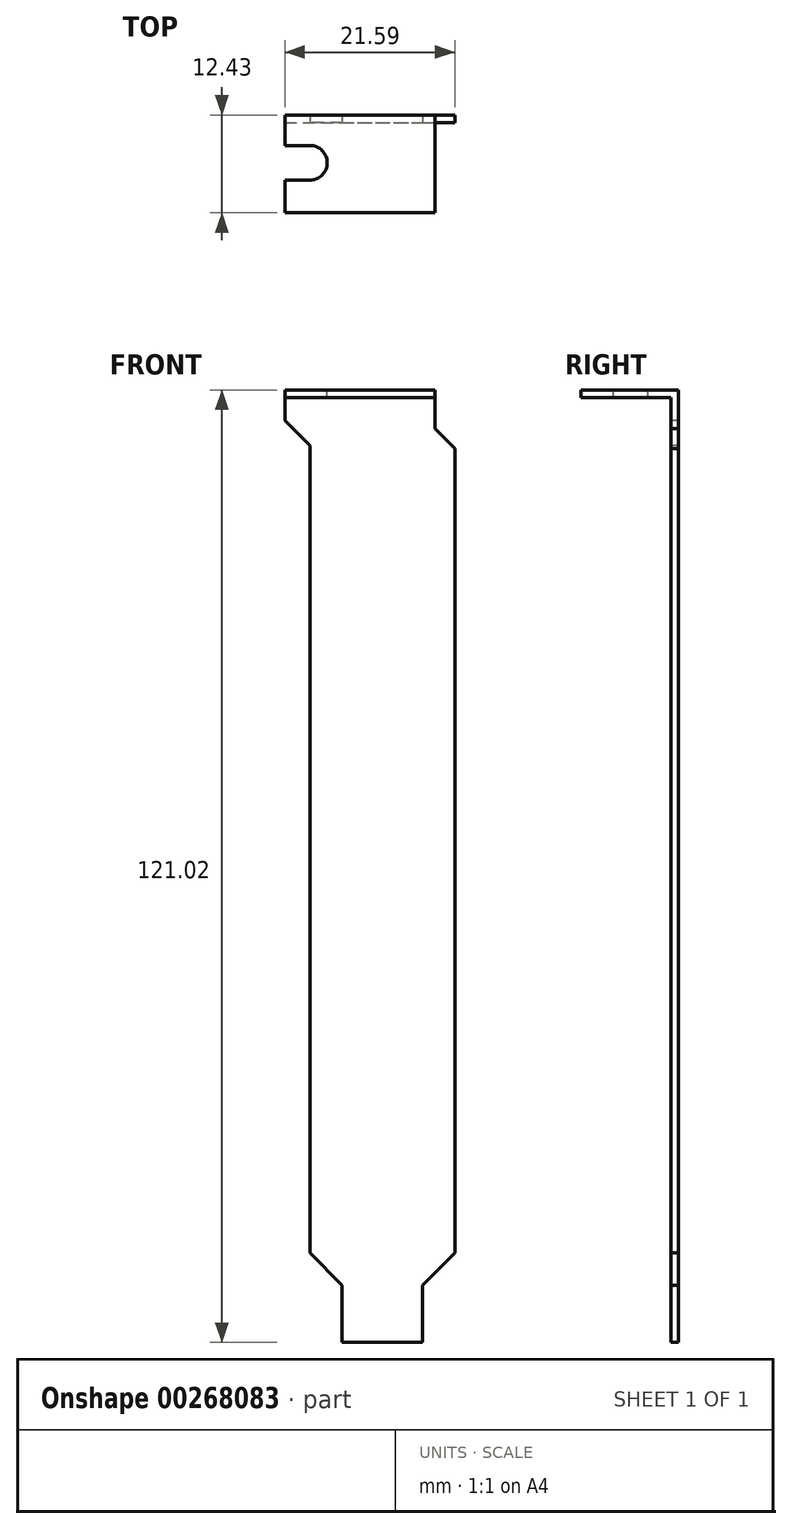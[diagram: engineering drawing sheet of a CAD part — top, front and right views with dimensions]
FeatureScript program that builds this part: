
annotation { "Feature Type Name" : "Feature", "Feature Type Description" : "" }
export const myFeature = defineFeature(function(context is Context, id is Id, definition is map)
    precondition{}
    {
        {
            assignVariable(context, id + "F0", {"name" : "BracketThickness", "anyValue" : 1 * mm});
        }
        {
            var Q0;
            Q0=qCreatedBy(makeId("Front.planeOp"),FACE);
            var sketch = newSketch(context, id + "F1", { "sketchPlane" : qUnion([Q0])});
            skLineSegment(sketch, "E0", {"start": v(-5.1, 0) * mm, "end": v(5.1, 0) * mm});
            skLineSegment(sketch, "E1", {"start": v(-5.1, 0) * mm, "end": v(-5.1, 7.27) * mm});
            skLineSegment(sketch, "E2", {"start": v(5.1, 0) * mm, "end": v(5.1, 7.27) * mm});
            skLineSegment(sketch, "E3", {"start": v(5.1, 7.27) * mm, "end": v(-5.1, 7.27) * mm, "construction": true});
            skLineSegment(sketch, "E4", {"start": v(-5.1, 7.27) * mm, "end": v(-9.21, 11.38) * mm});
            skLineSegment(sketch, "E5", {"start": v(-9.21, 11.38) * mm, "end": v(-9.21, 113.93) * mm});
            skLineSegment(sketch, "E6", {"start": v(5.1, 7.27) * mm, "end": v(9.2, 11.38) * mm});
            skLineSegment(sketch, "E7", {"start": v(9.2, 11.38) * mm, "end": v(9.2, 113.54) * mm});
            skLineSegment(sketch, "E8", {"start": v(9.21, 113.54) * mm, "end": v(6.67, 116.08) * mm});
            skLineSegment(sketch, "E9", {"start": v(6.67, 116.08) * mm, "end": v(6.67, 120.02) * mm});
            skLineSegment(sketch, "E10", {"start": v(6.67, 120.02) * mm, "end": v(-12.38, 120.02) * mm, "construction": true});
            skLineSegment(sketch, "E11", {"start": v(-12.38, 120.02) * mm, "end": v(-12.38, 117.1) * mm});
            skLineSegment(sketch, "E12", {"start": v(-12.38, 117.1) * mm, "end": v(-9.21, 113.93) * mm});
            skLineSegment(sketch, "E13", {"start": v(-9.21, 11.38) * mm, "end": v(9.2, 11.38) * mm, "construction": true});
            skLineSegment(sketch, "E14", {"start": v(-12.38, 120.02) * mm, "end": v(-12.38, 121.02) * mm});
            skLineSegment(sketch, "E15", {"start": v(-12.38, 121.02) * mm, "end": v(6.67, 121.02) * mm});
            skLineSegment(sketch, "E16", {"start": v(6.67, 121.02) * mm, "end": v(6.67, 120.02) * mm});
            skSolve(sketch);
        }
        {
            var Q0;
            Q0=makeQuery(id+"F1.imprint","IMPRINT",FACE,{"disambiguationData":[TD([[makeQuery(id+"F1.imprint","IMPRINT",EDGE,{"derivedFrom":sQuery(id+"F1.wireOp",EDGE,"E0")}),1.0]])]});
            extrude(context, id + "F2", {"entities" : qUnion([Q0]), "oppositeDirection" : true, "depth" : getVariable(context, 'BracketThickness')});
        }
        {
            var Q0;
            Q0=makeQuery(id+"F2.opExtrude","SWEPT_FACE",FACE,{"disambiguationData":[OSD([sQuery(id+"F1.wireOp",EDGE,"E15")])]});
            var sketch = newSketch(context, id + "F3", { "sketchPlane" : qUnion([Q0])});
            skLineSegment(sketch, "E17.bottom", {"start": v(-12.38, 0) * mm, "end": v(6.67, 0) * mm});
            skLineSegment(sketch, "E17.top", {"start": v(-12.38, -11.43) * mm, "end": v(6.67, -11.43) * mm});
            skLineSegment(sketch, "E17.left", {"start": v(-12.38, 0) * mm, "end": v(-12.38, -11.43) * mm});
            skLineSegment(sketch, "E17.right", {"start": v(6.67, 0) * mm, "end": v(6.67, -11.43) * mm});
            skLineSegment(sketch, "E18", {"start": v(-12.38, -2.87) * mm, "end": v(-9.2, -2.87) * mm});
            skLineSegment(sketch, "E19", {"start": v(-9.2, -2.87) * mm, "end": v(-9.2, -7.3) * mm, "construction": true});
            skLineSegment(sketch, "E20", {"start": v(-9.2, -7.3) * mm, "end": v(-12.38, -7.3) * mm});
            skArc(sketch, "E21", {"start": v(-9.2, -2.87) * mm, "mid": v(-7, -5.08) * mm, "end": v(-9.2, -7.3) * mm});
            skSolve(sketch);
        }
        {
            var Q0;
            {var subQ1=sQuery(id+"F3.wireOp",EDGE,"E17.bottom");Q0=makeQuery(id+"F3.imprint","IMPRINT",FACE,{"disambiguationData":[TD([[makeQuery(id+"F3.imprint","IMPRINT",EDGE,{"derivedFrom":subQ1}),-1.0]])]});}
            extrude(context, id + "F4", {"entities" : qUnion([Q0]), "operationType" : NewBodyOperationType.ADD, "oppositeDirection" : true, "depth" : getVariable(context, 'BracketThickness')});
        }
    });
